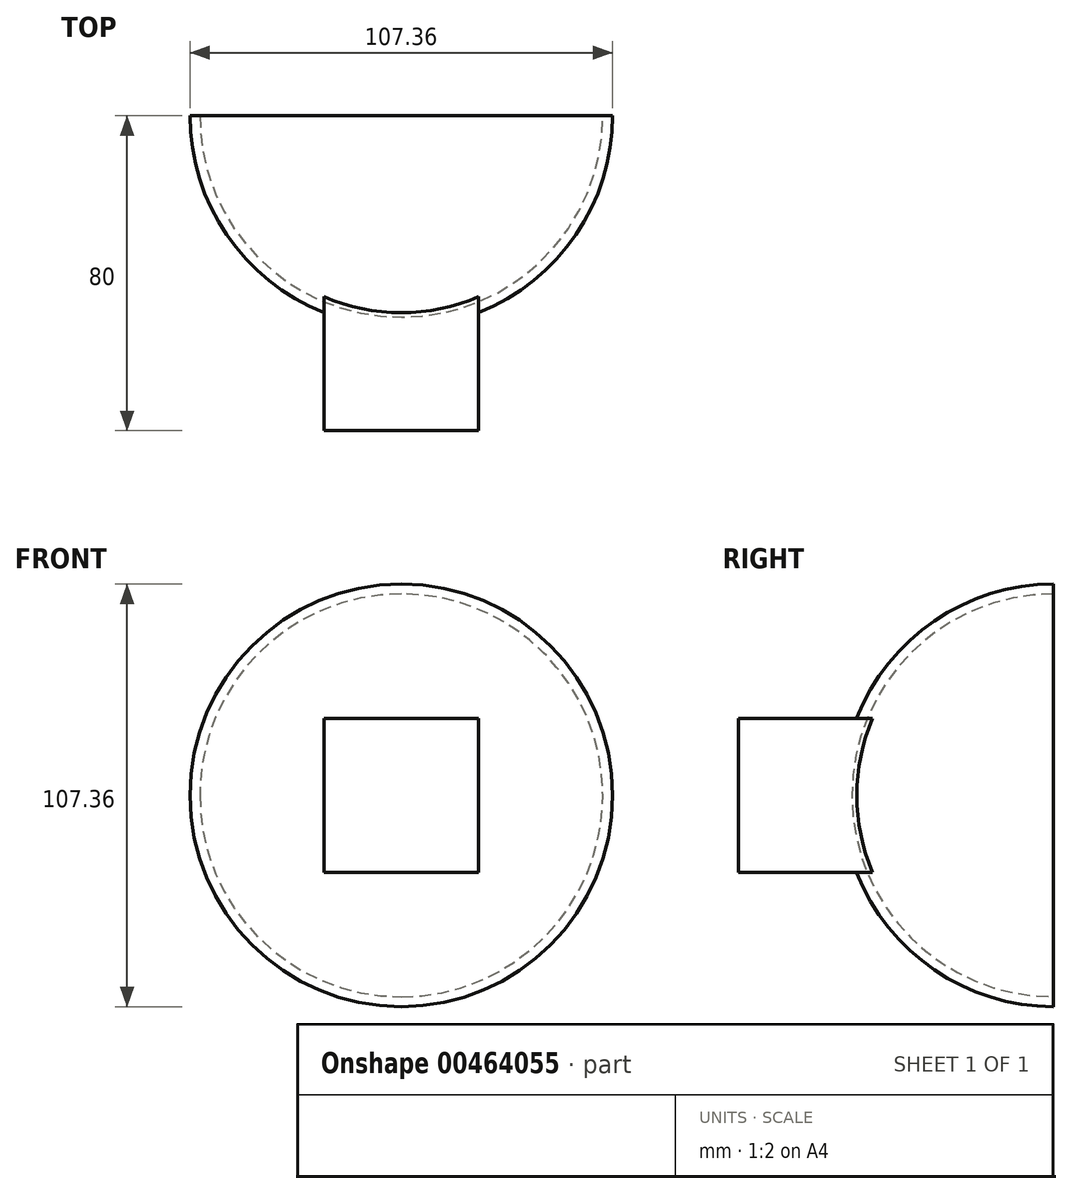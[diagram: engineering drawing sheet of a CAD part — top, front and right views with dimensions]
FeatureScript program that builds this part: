
annotation { "Feature Type Name" : "Feature", "Feature Type Description" : "" }
export const myFeature = defineFeature(function(context is Context, id is Id, definition is map)
    precondition{}
    {
        {
            var Q0;
            Q0=qCreatedBy(makeId("Front.planeOp"),FACE);
            var sketch = newSketch(context, id + "F0", { "sketchPlane" : qUnion([Q0])});
            skCircle(sketch, "E0", {"center": v(0, 0) * mm, "radius": 53.68 * mm});
            skLineSegment(sketch, "E1", {"start": v(0, 65.28) * mm, "end": v(0, -65.28) * mm, "construction": true});
            skLineSegment(sketch, "E2", {"start": v(0, 53.68) * mm, "end": v(0, -53.68) * mm});
            skSolve(sketch);
        }
        {
            var Q0;
            {var subQ0=sQuery(id+"F0.wireOp",EDGE,"E2");Q0=makeQuery(id+"F0.imprint","IMPRINT",FACE,{"disambiguationData":[TD([[makeQuery(id+"F0.imprint","IMPRINT",EDGE,{"derivedFrom":subQ0}),1.0]])]});}
            var Q1;
            Q1=sQuery(id+"F0.wireOp",EDGE,"E1");
            revolve(context, id + "F1", {"entities" : qUnion([Q0]), "axis" : qUnion([Q1]), "revolveType" : RevolveType.ONE_DIRECTION, "angle" : 180 * degree});
        }
        {
            var Q0;
            Q0=makeQuery(id+"F1.opRevolve","CAP_FACE",FACE,{"disambiguationData":[OSD([sQuery(id+"F0.wireOp",EDGE,"E0"),sQuery(id+"F0.wireOp",EDGE,"E2")])],"isStart":true});
            shell(context, id + "F2", {"entities" : qUnion([Q0]), "thickness" : 2.5 * mm});
        }
        {
            var Q0;
            Q0=qCreatedBy(makeId("Front.planeOp"),FACE);
            cPlane(context, id + "F3", {"entities" : qUnion([Q0]), "cplaneType" : CPlaneType.OFFSET, "offset" : 80 * mm, "width" : 150 * mm, "height" : 150 * mm});
        }
        {
            var Q0;
            Q0=qCreatedBy(id+"F3.planeOp",FACE);
            var sketch = newSketch(context, id + "F4", { "sketchPlane" : qUnion([Q0])});
            skLineSegment(sketch, "E3.bottom", {"start": v(-19.66, 19.51) * mm, "end": v(19.66, 19.51) * mm});
            skLineSegment(sketch, "E3.top", {"start": v(-19.66, -19.51) * mm, "end": v(19.66, -19.51) * mm});
            skLineSegment(sketch, "E3.left", {"start": v(-19.66, 19.51) * mm, "end": v(-19.66, -19.51) * mm});
            skLineSegment(sketch, "E3.right", {"start": v(19.66, 19.51) * mm, "end": v(19.66, -19.51) * mm});
            skPoint(sketch, "E3.middle", {"position": v(0, 0) * mm});
            skSolve(sketch);
        }
        {
            var Q0;
            Q0 = qSketchRegion(id + "F4", true);
            var Q1;
            Q1=makeQuery(id+"F1.opRevolve","SWEPT_FACE",FACE,{"disambiguationData":[OSD([sQuery(id+"F0.wireOp",EDGE,"E0")])]});
            extrude(context, id + "F5", {"entities" : qUnion([Q0]), "operationType" : NewBodyOperationType.ADD, "endBound" : BoundingType.UP_TO_SURFACE, "oppositeDirection" : true, "endBoundEntityFace" : qUnion([Q1]), "depth" : 25 * mm});
        }
    });
